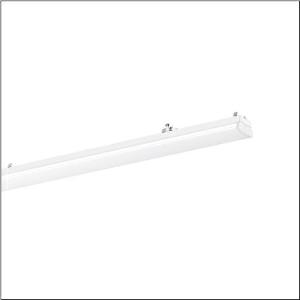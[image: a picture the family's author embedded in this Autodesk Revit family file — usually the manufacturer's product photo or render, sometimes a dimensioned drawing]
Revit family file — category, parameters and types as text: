
# Revit family: licross_r__11_recessed_opal_mo_51tl1d7n46xg_f8f9
name_source: partatom
category: Lighting Fixtures
units: mm (PartAtom-declared; Revit-internal decimal feet)

## family parameters
Cut with Voids When Loaded = No
Host = Face
Light Source = No
Part Type = Normal
Room Calculation Point = No
Round Connector Dimension = Use Diameter
Shared = No

## types (1)
- Licross® 11 recessed opal MO (1 x LED, 6300 lm, 35.1 W, 4000K)
    Apparent Load = 35 VA
    CIE Flux Codes = 44 73 91 87 100
    Color Rendering = 80
    Color Temperature = 4000K
    Default Elevation = 1800 mm
    Description = Licross® 11 recessed opal MO, luminaire insert, of sheet steel, coil coated, white, length: 1.500mm, width: 76mm, height: 87mm, LED rated luminous flux: 6.300lm, light colour: 840, control gear: ON/OFF, with plug, 3-pole, with phase selection, mains connection: 220..240V, AC, 50/60Hz, rated input power: 35W, halogen-free wiring, primary optical cover: cover, of PMMA, light emission: direct with ceiling illumination distribution, primary light characteristic: symmetric, protection rating (complete): IP40, insulation class (complete): insulation class I (protective earthing), certification: CE, ENEC, VDE, UKCA, protection symbol: D if used in an environment without relevant dust loads with corresponding accessories, impact resistance: IK06, permissible ambient temperature for indoor applications: -35..+45°C, corresponds to IFS (International Featured Standards) requirements for safety and quality in the food industry, reducing of maximum allowable ambient temperature of 5°C with ceiling mounting, packaging unit: 1 piece
    Height = 83 mm
    Lamp = 1 x LED
    Lamp Light Flux = 6300 lm
    Lamp Power = 35.1 W
    Lamp count = 1
    Length = 1500 mm
    Luminous efficacy = 179 lm/W
    Manufacturer = Siteco
    ModVariant = No
    Model = 51TL1D7N46XG
    Mounting Place = Ceiling
    Mounting Type = Pendant
    Number of Poles = 1
    OnlyDefault = Yes
    Power Factor = 1
    Product Name = Licross® 11 recessed opal MO
    Product group = luminaire insert
    ProductGroupID = 901
    Protection Class = Protection class I
    Protection Degree = IP 40
    RLX_Detail_Level = 1
    RLX_Emergency_Light_Flux = 0 lm
    RLX_Emergency_Type = 0
    RLX_Emergency_Type_DB = No
    RlxData = <blob elided: 14493 chars, md5=da9ee6f5>
    Socket = socket
    Standby Power = 0 W
    System Light Flux = 6300 lm
    System Power = 35 W
    Type Comments = Product without accessories
    Type Image = l_1313666.jpg
    URL = http://relux.com
    VarID = ---
    Voltage = 0 V
    Weight = 0.00 kg
    Width = 76 mm

## geometry (parser evidence)
native form markers: Sweep x13
no freeform markers — native parametric forms only
